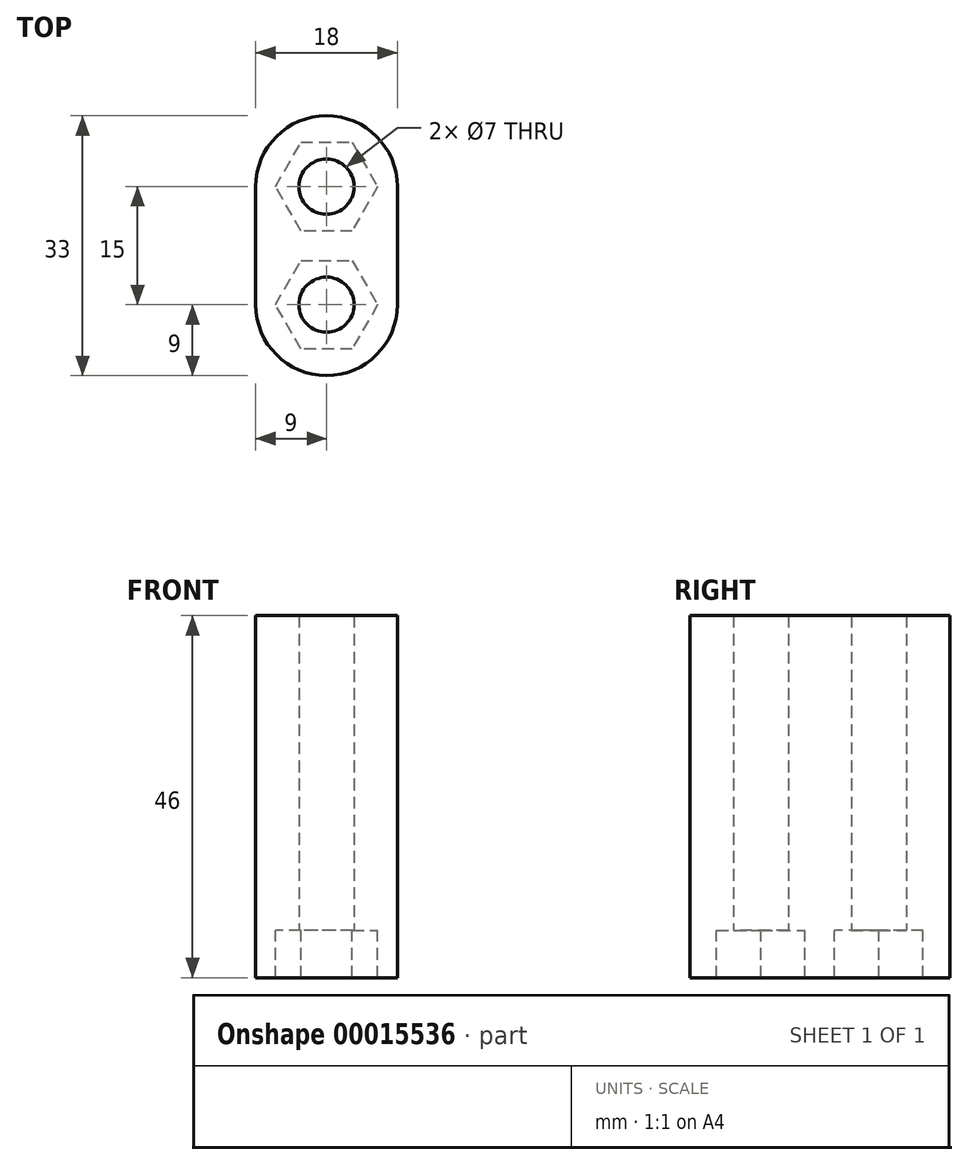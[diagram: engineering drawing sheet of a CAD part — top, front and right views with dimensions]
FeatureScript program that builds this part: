
annotation { "Feature Type Name" : "Feature", "Feature Type Description" : "" }
export const myFeature = defineFeature(function(context is Context, id is Id, definition is map)
    precondition{}
    {
        {
            var Q0;
            Q0=qCreatedBy(makeId("Top.planeOp"),FACE);
            var sketch = newSketch(context, id + "F0", { "sketchPlane" : qUnion([Q0])});
            skLineSegment(sketch, "E0", {"start": v(0, 7.5) * mm, "end": v(0, -7.5) * mm, "construction": true});
            skCircle(sketch, "E1", {"center": v(0, 7.5) * mm, "radius": 3.5 * mm});
            skCircle(sketch, "E2", {"center": v(0, -7.5) * mm, "radius": 3.5 * mm});
            skCircle(sketch, "E3", {"center": v(0, 7.5) * mm, "radius": 9 * mm});
            skCircle(sketch, "E4", {"center": v(0, -7.5) * mm, "radius": 9 * mm});
            skLineSegment(sketch, "E5", {"start": v(-9, -7.5) * mm, "end": v(-9, 7.5) * mm});
            skLineSegment(sketch, "E6", {"start": v(9, -7.5) * mm, "end": v(9, 7.5) * mm});
            skCircle(sketch, "E7.cCircle", {"center": v(0, 7.5) * mm, "radius": 6.5 * mm, "construction": true});
            skLineSegment(sketch, "E7.0", {"start": v(6.5, 7.5) * mm, "end": v(3.25, 1.87) * mm});
            skLineSegment(sketch, "E7.1", {"start": v(3.25, 1.87) * mm, "end": v(-3.25, 1.87) * mm});
            skLineSegment(sketch, "E7.2", {"start": v(-3.25, 1.87) * mm, "end": v(-6.5, 7.5) * mm});
            skLineSegment(sketch, "E7.3", {"start": v(-6.5, 7.5) * mm, "end": v(-3.25, 13.13) * mm});
            skLineSegment(sketch, "E7.4", {"start": v(-3.25, 13.13) * mm, "end": v(3.25, 13.13) * mm});
            skLineSegment(sketch, "E7.5", {"start": v(3.25, 13.13) * mm, "end": v(6.5, 7.5) * mm});
            skCircle(sketch, "E8.cCircle", {"center": v(0, -7.5) * mm, "radius": 6.5 * mm, "construction": true});
            skLineSegment(sketch, "E8.0", {"start": v(-3.25, -13.13) * mm, "end": v(-6.5, -7.5) * mm});
            skLineSegment(sketch, "E8.1", {"start": v(-6.5, -7.5) * mm, "end": v(-3.25, -1.87) * mm});
            skLineSegment(sketch, "E8.2", {"start": v(-3.25, -1.87) * mm, "end": v(3.25, -1.87) * mm});
            skLineSegment(sketch, "E8.3", {"start": v(3.25, -1.87) * mm, "end": v(6.5, -7.5) * mm});
            skLineSegment(sketch, "E8.4", {"start": v(6.5, -7.5) * mm, "end": v(3.25, -13.13) * mm});
            skLineSegment(sketch, "E8.5", {"start": v(3.25, -13.13) * mm, "end": v(-3.25, -13.13) * mm});
            skSolve(sketch);
        }
        {
            var Q0;
            Q0=qCreatedBy(makeId("Top.planeOp"),FACE);
            var sketch = newSketch(context, id + "F1", { "sketchPlane" : qUnion([Q0])});
            skLineSegment(sketch, "E9.0", {"start": v(-9, -7.5) * mm, "end": v(-9, 7.5) * mm});
            skArc(sketch, "E9.1", {"start": v(9, 7.5) * mm, "mid": v(0, 16.5) * mm, "end": v(-9, 7.5) * mm});
            skArc(sketch, "E9.2", {"start": v(-9, -7.5) * mm, "mid": v(0, -16.5) * mm, "end": v(9, -7.5) * mm});
            skLineSegment(sketch, "E9.3", {"start": v(9, -7.5) * mm, "end": v(9, 7.5) * mm});
            skCircle(sketch, "E9.4", {"center": v(0, 7.5) * mm, "radius": 3.5 * mm});
            skCircle(sketch, "E9.5", {"center": v(0, -7.5) * mm, "radius": 3.5 * mm});
            skSolve(sketch);
        }
        {
            var Q0;
            Q0 = qSketchRegion(id + "F1", true);
            extrude(context, id + "F2", {"entities" : qUnion([Q0]), "depth" : 40 * mm});
        }
        {
            var Q0;
            {var subQ0=sQuery(id+"F0.wireOp",EDGE,"E5");Q0=makeQuery(id+"F0.imprint","IMPRINT",FACE,{"disambiguationData":[TD([[makeQuery(id+"F0.imprint","IMPRINT",EDGE,{"derivedFrom":subQ0}),-1.0]])]});}
            var sketch = newSketch(context, id + "F3", { "sketchPlane" : qUnion([Q0])});
            skLineSegment(sketch, "E10.0", {"start": v(9, -7.5) * mm, "end": v(9, 7.5) * mm});
            skArc(sketch, "E10.1", {"start": v(9, 7.5) * mm, "mid": v(0, 16.5) * mm, "end": v(-9, 7.5) * mm});
            skArc(sketch, "E10.2", {"start": v(-9, -7.5) * mm, "mid": v(0, -16.5) * mm, "end": v(9, -7.5) * mm});
            skLineSegment(sketch, "E10.3", {"start": v(-9, -7.5) * mm, "end": v(-9, 7.5) * mm});
            skLineSegment(sketch, "E10.4", {"start": v(3.25, 1.87) * mm, "end": v(-3.25, 1.87) * mm});
            skLineSegment(sketch, "E10.5", {"start": v(-3.25, 1.87) * mm, "end": v(-6.5, 7.5) * mm});
            skLineSegment(sketch, "E10.6", {"start": v(-6.5, 7.5) * mm, "end": v(-3.25, 13.13) * mm});
            skLineSegment(sketch, "E10.7", {"start": v(-3.25, 13.13) * mm, "end": v(3.25, 13.13) * mm});
            skLineSegment(sketch, "E10.8", {"start": v(3.25, 13.13) * mm, "end": v(6.5, 7.5) * mm});
            skLineSegment(sketch, "E10.9", {"start": v(6.5, 7.5) * mm, "end": v(3.25, 1.87) * mm});
            skLineSegment(sketch, "E10.10", {"start": v(-3.25, -1.87) * mm, "end": v(3.25, -1.87) * mm});
            skLineSegment(sketch, "E10.11", {"start": v(3.25, -1.87) * mm, "end": v(6.5, -7.5) * mm});
            skLineSegment(sketch, "E10.12", {"start": v(6.5, -7.5) * mm, "end": v(3.25, -13.13) * mm});
            skLineSegment(sketch, "E10.13", {"start": v(3.25, -13.13) * mm, "end": v(-3.25, -13.13) * mm});
            skLineSegment(sketch, "E10.14", {"start": v(-3.25, -13.13) * mm, "end": v(-6.5, -7.5) * mm});
            skLineSegment(sketch, "E10.15", {"start": v(-6.5, -7.5) * mm, "end": v(-3.25, -1.87) * mm});
            skSolve(sketch);
        }
        {
            var Q0;
            Q0 = qSketchRegion(id + "F3", true);
            extrude(context, id + "F4", {"entities" : qUnion([Q0]), "operationType" : NewBodyOperationType.ADD, "oppositeDirection" : true, "depth" : 6 * mm});
        }
    });
